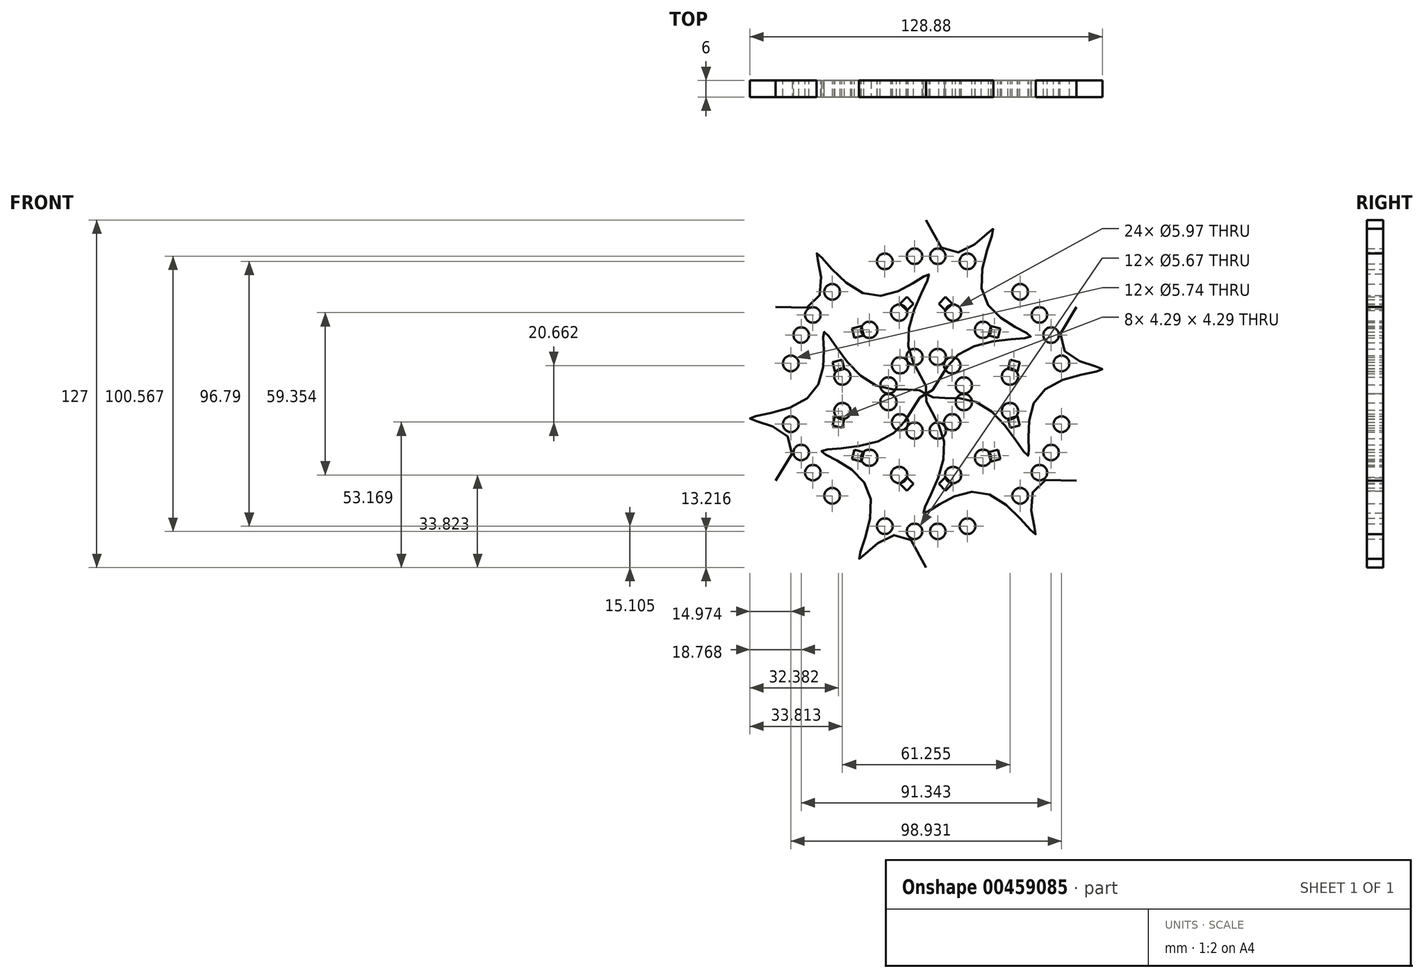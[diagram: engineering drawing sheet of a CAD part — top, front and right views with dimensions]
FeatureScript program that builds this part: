
annotation { "Feature Type Name" : "Feature", "Feature Type Description" : "" }
export const myFeature = defineFeature(function(context is Context, id is Id, definition is map)
    precondition{}
    {
        {
            var Q0;
            Q0=qCreatedBy(makeId("Front.planeOp"),FACE);
            var sketch = newSketch(context, id + "F0", { "sketchPlane" : qUnion([Q0])});
            skLineSegment(sketch, "E0", {"start": v(0, 0) * mm, "end": v(0, 63.5) * mm, "construction": true});
            skFitSpline(sketch, "E1", {"points": [v(0, 63.5) * mm, v(24.08, 60.2) * mm, v(20.77, 36.12) * mm, v(38.24, 21.01) * mm, v(13.22, 15.34) * mm, v(0, 0) * mm], "startDerivative": vector(109.85, -351.53) * mm, "endDerivative": vector(-58.82, 1.97) * mm});
            skCircle(sketch, "E2", {"center": v(20.77, 23.37) * mm, "radius": 2.99 * mm});
            skCircle(sketch, "E3", {"center": v(15.1, 48.4) * mm, "radius": 2.87 * mm});
            skCircle(sketch, "E4", {"center": v(4.25, 13.46) * mm, "radius": 2.99 * mm});
            skCircle(sketch, "E5", {"center": v(4.25, 50.28) * mm, "radius": 2.83 * mm});
            skLineSegment(sketch, "E6.bottom", {"start": v(4.6, 32.93) * mm, "end": v(7.08, 35.4) * mm});
            skLineSegment(sketch, "E6.top", {"start": v(7.08, 30.45) * mm, "end": v(9.56, 32.93) * mm});
            skLineSegment(sketch, "E6.left", {"start": v(4.6, 32.93) * mm, "end": v(7.08, 30.45) * mm});
            skLineSegment(sketch, "E6.right", {"start": v(7.08, 35.4) * mm, "end": v(9.56, 32.93) * mm});
            skLineSegment(sketch, "E7.MirrorCS", {"start": v(-7.08, 30.45) * mm, "end": v(-9.56, 32.93) * mm});
            skLineSegment(sketch, "E8.MirrorCS", {"start": v(-4.6, 32.93) * mm, "end": v(-7.08, 30.45) * mm});
            skLineSegment(sketch, "E9.MirrorCS", {"start": v(-7.08, 35.4) * mm, "end": v(-9.56, 32.93) * mm});
            skLineSegment(sketch, "E10.MirrorCS", {"start": v(-4.6, 32.93) * mm, "end": v(-7.08, 35.4) * mm});
            skCircle(sketch, "E11.MirrorC", {"center": v(-20.77, 23.37) * mm, "radius": 2.99 * mm});
            skCircle(sketch, "E12.MirrorC", {"center": v(-15.1, 48.4) * mm, "radius": 2.87 * mm});
            skCircle(sketch, "E13.MirrorC", {"center": v(-4.25, 13.46) * mm, "radius": 2.99 * mm});
            skCircle(sketch, "E14.MirrorC", {"center": v(-4.25, 50.28) * mm, "radius": 2.83 * mm});
            skFitSpline(sketch, "E15.MirrorCS", {"points": [v(0, 63.5) * mm, v(-24.08, 60.2) * mm, v(-20.77, 36.12) * mm, v(-38.24, 21.01) * mm, v(-13.22, 15.34) * mm, v(0, 0) * mm], "startDerivative": vector(-109.85, -351.53) * mm, "endDerivative": vector(58.82, 1.97) * mm});
            skSolve(sketch);
        }
        {
            var Q0;
            Q0 = qSketchRegion(id + "F0", true);
            extrude(context, id + "F1", {"entities" : qUnion([Q0]), "depth" : 6 * mm});
        }
        {
            var Q0;
            Q0=qCreatedBy(makeId("Right.planeOp"),FACE);
            var sketch = newSketch(context, id + "F2", { "sketchPlane" : qUnion([Q0])});
            skLineSegment(sketch, "E16", {"start": v(0, 0) * mm, "end": v(-63.3, 0) * mm, "construction": true});
            skSolve(sketch);
        }
        {
            var Q0;
            Q0=makeQuery(id+"F1.opExtrude","SWEPT_BODY",BODY,{"disambiguationData":[OSD([sQuery(id+"F0.wireOp",EDGE,"E1"),sQuery(id+"F0.wireOp",EDGE,"E2"),sQuery(id+"F0.wireOp",EDGE,"E3"),sQuery(id+"F0.wireOp",EDGE,"E4"),sQuery(id+"F0.wireOp",EDGE,"E5"),sQuery(id+"F0.wireOp",EDGE,"E6.bottom"),sQuery(id+"F0.wireOp",EDGE,"E6.top"),sQuery(id+"F0.wireOp",EDGE,"E6.left"),sQuery(id+"F0.wireOp",EDGE,"E6.right"),sQuery(id+"F0.wireOp",EDGE,"E7.MirrorCS"),sQuery(id+"F0.wireOp",EDGE,"E8.MirrorCS"),sQuery(id+"F0.wireOp",EDGE,"E9.MirrorCS"),sQuery(id+"F0.wireOp",EDGE,"E10.MirrorCS"),sQuery(id+"F0.wireOp",EDGE,"E11.MirrorC"),sQuery(id+"F0.wireOp",EDGE,"E12.MirrorC"),sQuery(id+"F0.wireOp",EDGE,"E13.MirrorC"),sQuery(id+"F0.wireOp",EDGE,"E14.MirrorC"),sQuery(id+"F0.wireOp",EDGE,"E15.MirrorCS")])]});
            var Q1;
            Q1=sQuery(id+"F2.wireOp",EDGE,"E16");
            circularPattern(context, id + "F3", {"entities" : qUnion([Q0]), "axis" : qUnion([Q1]), "angle" : 360 * degree, "instanceCount" : 6, "equalSpace" : true});
        }
    });
